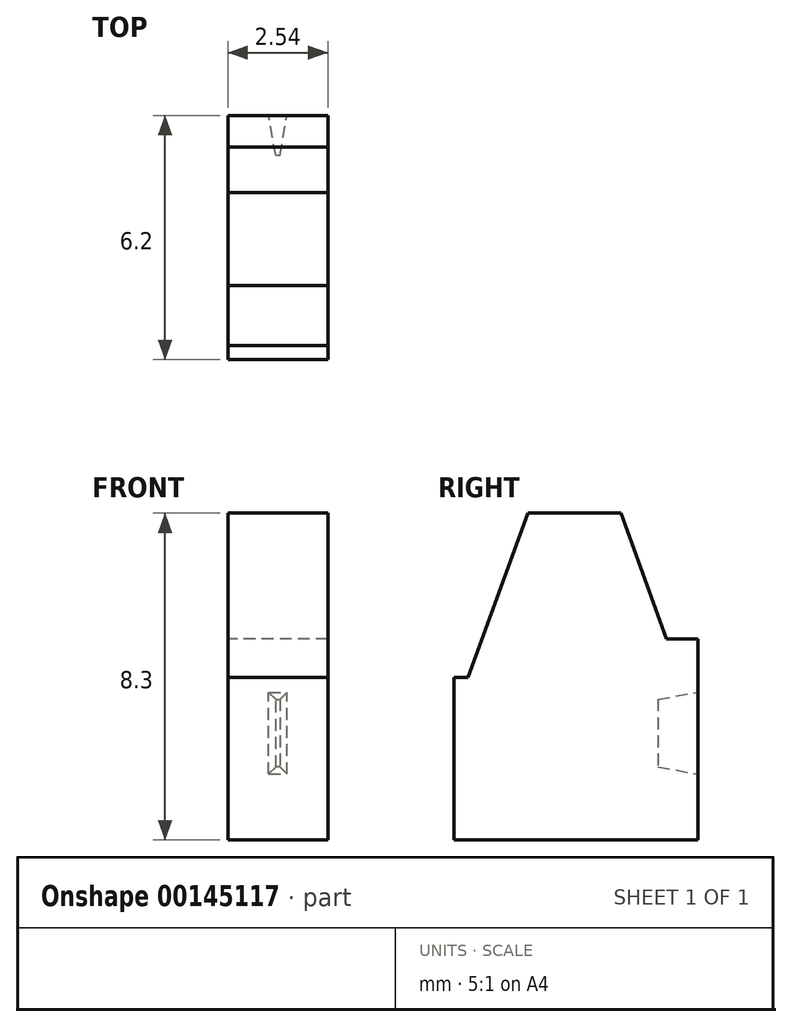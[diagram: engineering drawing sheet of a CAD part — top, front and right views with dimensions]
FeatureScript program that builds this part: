
annotation { "Feature Type Name" : "Feature", "Feature Type Description" : "" }
export const myFeature = defineFeature(function(context is Context, id is Id, definition is map)
    precondition{}
    {
        {
            var Q0;
            Q0=qCreatedBy(makeId("Right.planeOp"),FACE);
            var sketch = newSketch(context, id + "F0", { "sketchPlane" : qUnion([Q0])});
            skLineSegment(sketch, "E0", {"start": v(-6.2, 4.12) * mm, "end": v(-6.2, 0) * mm});
            skLineSegment(sketch, "E1", {"start": v(-6.2, 0) * mm, "end": v(0, 0) * mm});
            skLineSegment(sketch, "E2", {"start": v(0, 0) * mm, "end": v(0, 5.1) * mm});
            skLineSegment(sketch, "E3", {"start": v(0, 5.1) * mm, "end": v(-0.8, 5.1) * mm});
            skLineSegment(sketch, "E4", {"start": v(-0.8, 5.1) * mm, "end": v(-1.96, 8.3) * mm});
            skLineSegment(sketch, "E5", {"start": v(-1.96, 8.3) * mm, "end": v(-4.32, 8.3) * mm});
            skLineSegment(sketch, "E6", {"start": v(-6.2, 4.12) * mm, "end": v(-5.84, 4.12) * mm});
            skLineSegment(sketch, "E7", {"start": v(-5.84, 4.12) * mm, "end": v(-4.32, 8.3) * mm});
            skSolve(sketch);
        }
        {
            var Q0;
            Q0=makeQuery(id+"F0.imprint","IMPRINT",FACE,{"disambiguationData":[TD([[makeQuery(id+"F0.imprint","IMPRINT",EDGE,{"derivedFrom":sQuery(id+"F0.wireOp",EDGE,"E0")}),1.0]])]});
            extrude(context, id + "F1", {"entities" : qUnion([Q0]), "endBound" : BoundingType.SYMMETRIC, "depth" : 2.54 * mm});
        }
        {
            var Q0;
            Q0=makeQuery(id+"F1.opExtrude","SWEPT_FACE",FACE,{"disambiguationData":[OSD([sQuery(id+"F0.wireOp",EDGE,"E2")])]});
            var sketch = newSketch(context, id + "F2", { "sketchPlane" : qUnion([Q0])});
            skLineSegment(sketch, "E8.bottom", {"start": v(-0.95, 4.47) * mm, "end": v(0.95, 4.47) * mm});
            skLineSegment(sketch, "E8.top", {"start": v(-0.95, 0.96) * mm, "end": v(0.95, 0.96) * mm});
            skLineSegment(sketch, "E8.left", {"start": v(-0.95, 4.47) * mm, "end": v(-0.95, 0.96) * mm});
            skLineSegment(sketch, "E8.right", {"start": v(0.95, 4.47) * mm, "end": v(0.95, 0.96) * mm});
            skPoint(sketch, "E8.middle", {"position": v(0, 2.71) * mm});
            skSolve(sketch);
        }
        {
            var Q0;
            Q0 = qSketchRegion(id + "F2", true);
            extrude(context, id + "F3", {"entities" : qUnion([Q0]), "operationType" : NewBodyOperationType.REMOVE, "oppositeDirection" : true, "depth" : 1.02 * mm});
        }
        {
            var Q0;
            Q0=makeQuery(id+"F3.boolean.opBoolean","COPY",FACE,{"derivedFrom":makeQuery(id+"F3.opExtrude","CAP_FACE",FACE,{"disambiguationData":[OSD([sQuery(id+"F2.wireOp",EDGE,"E8.bottom"),sQuery(id+"F2.wireOp",EDGE,"E8.top"),sQuery(id+"F2.wireOp",EDGE,"E8.left"),sQuery(id+"F2.wireOp",EDGE,"E8.right")])],"isStart":false})});
            chamfer(context, id + "F4", {"entities" : qUnion([Q0]), "chamferType" : ChamferType.OFFSET_ANGLE, "width" : 5.08 * mm, "oppositeDirection" : false, "angle" : 10 * degree, "tangentPropagation" : true});
        }
    });
